# Revit family: QF_BOURGEAT_4GN_bain_marie mobile_sans_etuve_cuve_separees
name_source: partatom
category: Equipement spécialisé
revit_build: Autodesk Revit 2015 (Build: 20140606_1530(x64)
units: mm (PartAtom-declared; Revit-internal decimal feet)

## types (2) — shared parameters
Diamètre de Raccordement Evacuation = 27 mm
Fabricant = BOURGEAT
Fréquence = 50 Hz
Hauteur hors tout = 900 mm  [stored 2.95276 ft]
Indice de protection = 33
Intensité nominale = 12 A
Nature isolant = 30mm laine de roche
Phase = 2
Puissance électrique  = 2800 W
Spécification du Fabricant = bain-marie mobiles
Tension = 230 V
URL catalogue = http://www.bourgeat.fr

## per-type parameters (varying)
| type | Charge max | Longueur hors tout | Modèle | Poids net à vide | Profondeur hors tout | commande_grand_cote | commande_petit_cote | lg_barre_transport |
| commandes_petit_cote | 120.00 kg | 1663 mm  [stored 5.45604 ft] | 872014 | 75.00 kg | 691 mm  [stored 2.26706 ft] | Non | Oui | 635 mm |
| commande_grand_cote | 70.00 kg | 1608 mm  [stored 5.27559 ft] | 872314 | 120.00 kg | 747 mm  [stored 2.45079 ft] | Oui | Non | 566 mm  [stored 1.85696 ft] |

note: [stored X ft] marks values corroborated as IEEE doubles in the binary element streams (Revit-internal decimal feet)
